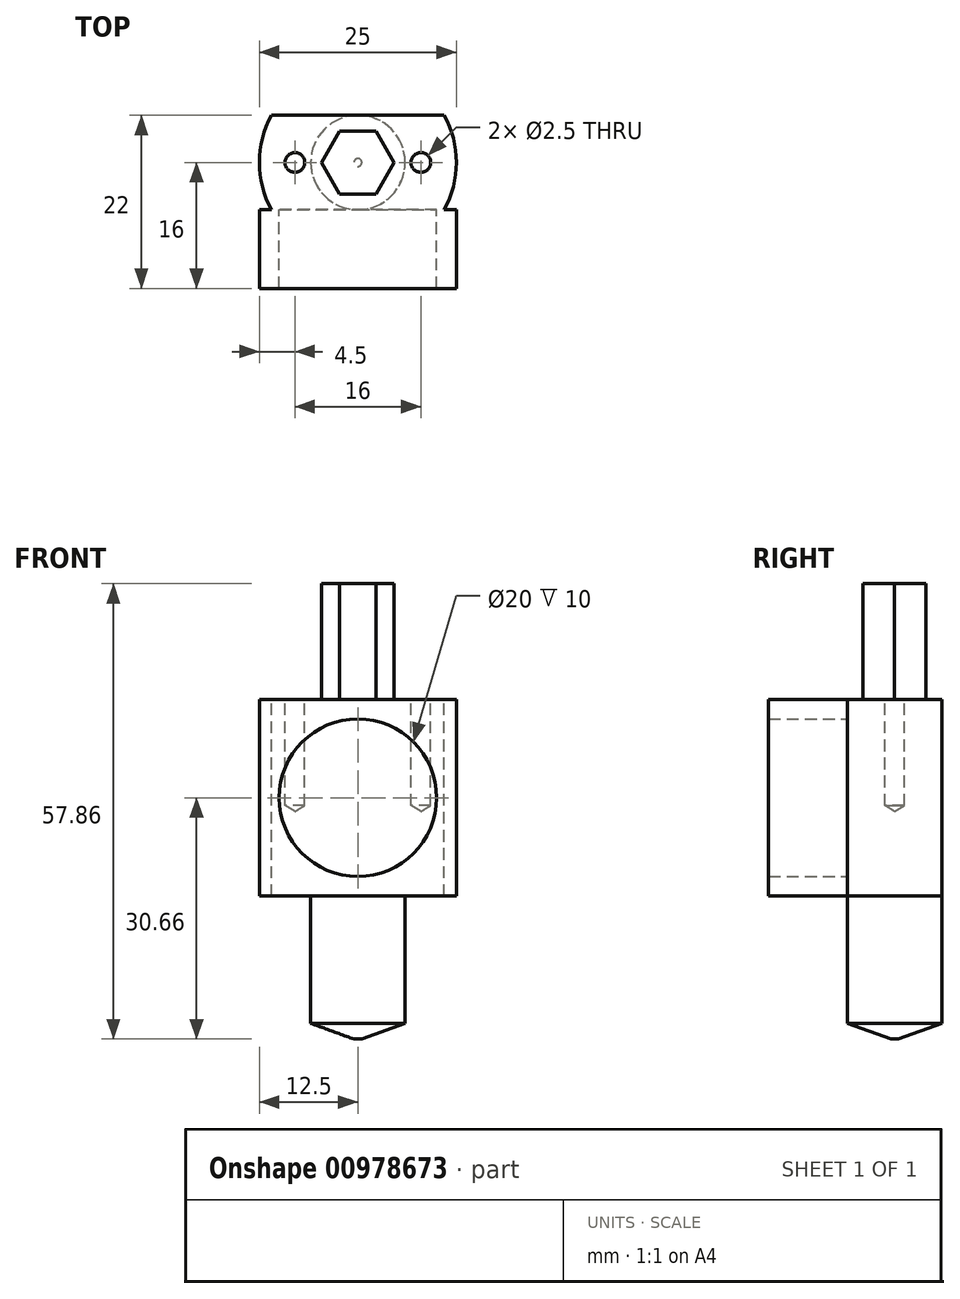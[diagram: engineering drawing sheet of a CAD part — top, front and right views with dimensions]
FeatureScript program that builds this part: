
annotation { "Feature Type Name" : "Feature", "Feature Type Description" : "" }
export const myFeature = defineFeature(function(context is Context, id is Id, definition is map)
    precondition{}
    {
        {
            var Q0;
            Q0=qCreatedBy(makeId("Top.planeOp"),FACE);
            var sketch = newSketch(context, id + "F0", { "sketchPlane" : qUnion([Q0])});
            skCircle(sketch, "E0", {"center": v(0, 0) * mm, "radius": 12.5 * mm});
            skLineSegment(sketch, "E1.bottom", {"start": v(-13, 6) * mm, "end": v(13, 6) * mm});
            skLineSegment(sketch, "E1.top", {"start": v(-13, -6) * mm, "end": v(13, -6) * mm});
            skLineSegment(sketch, "E1.left", {"start": v(-13, 6) * mm, "end": v(-13, -6) * mm});
            skLineSegment(sketch, "E1.right", {"start": v(13, 6) * mm, "end": v(13, -6) * mm});
            skPoint(sketch, "E2", {"position": v(0, 6) * mm});
            skPoint(sketch, "E3", {"position": v(-13, 0) * mm});
            skLineSegment(sketch, "E4", {"start": v(0, 6) * mm, "end": v(0, 0) * mm, "construction": true});
            skLineSegment(sketch, "E5", {"start": v(-13, 0) * mm, "end": v(0, 0) * mm, "construction": true});
            skSolve(sketch);
        }
        {
            var Q0;
            {var subQ0=sQuery(id+"F0.wireOp",EDGE,"E1.bottom");var subQ1=sQuery(id+"F0.wireOp",EDGE,"E0");var subQ2=makeQuery(id+"F0.imprint","INTERSECT",VERTEX,{"disambiguationData":[OD(0.0)],"derivedFrom":[subQ1,subQ0]});Q0=makeQuery(id+"F0.imprint","IMPRINT",FACE,{"disambiguationData":[TD([[makeQuery(id+"F0.imprint","IMPRINT",EDGE,{"disambiguationData":[TD([[subQ2,-1.0]])],"derivedFrom":subQ1}),1.0]])]});}
            extrude(context, id + "F1", {"entities" : qUnion([Q0]), "oppositeDirection" : true, "depth" : 25 * mm, "offsetDistance" : 25 * mm});
        }
        {
            var Q0;
            Q0=makeQuery(id+"F1.opExtrude","CAP_FACE",FACE,{"disambiguationData":[OSD([sQuery(id+"F0.wireOp",EDGE,"E0"),sQuery(id+"F0.wireOp",EDGE,"E1.bottom"),sQuery(id+"F0.wireOp",EDGE,"E1.top")])],"isStart":true});
            var sketch = newSketch(context, id + "F2", { "sketchPlane" : qUnion([Q0])});
            skLineSegment(sketch, "E6", {"start": v(-8, 0) * mm, "end": v(8, 0) * mm, "construction": true});
            skPoint(sketch, "E7", {"position": v(0, 0) * mm});
            skSolve(sketch);
        }
        {
            var Q0;
            Q0=sQuery(id+"F2.wireOp",VERTEX,"E6.start");
            var Q1;
            Q1=sQuery(id+"F2.wireOp",VERTEX,"E6.end");
            var Q2;
            Q2=makeQuery(id+"F1.opExtrude","SWEPT_BODY",BODY,{"disambiguationData":[OSD([sQuery(id+"F0.wireOp",EDGE,"E0"),sQuery(id+"F0.wireOp",EDGE,"E1.bottom"),sQuery(id+"F0.wireOp",EDGE,"E1.top")])]});
            hole(context, id + "F3", {"style" : HoleStyle.SIMPLE, "endStyle" : HoleEndStyle.BLIND, "standardTappedOrClearance" : lookupTablePath({ "standard" : "ISO", "engagement" : "75%", "pitch" : "0.5 mm", "size" : "M3", "type" : "Tapped" }), "standardBlindInLast" : lookupTablePath({ "standard" : "ISO", "fit" : "Normal", "engagement" : "75%", "pitch" : "0.5 mm", "size" : "M3", "type" : "Clearance & tapped" }), "holeDiameter" : 2.5 * mm, "majorDiameter" : 3 * mm, "showTappedDepth" : true, "holeDepth" : 13.5 * mm, "isTappedThrough" : true, "tappedDepth" : 12 * mm, "tapClearance" : 3, "startFromSketch" : true, "locations" : qUnion([Q0, Q1]), "scope" : qUnion([Q2])});
        }
        {
            var Q0;
            Q0=makeQuery(id+"F1.opExtrude","SWEPT_FACE",FACE,{"disambiguationData":[OSD([sQuery(id+"F0.wireOp",EDGE,"E1.top")])]});
            var sketch = newSketch(context, id + "F4", { "sketchPlane" : qUnion([Q0])});
            skLineSegment(sketch, "E8.bottom", {"start": v(-12.5, 0) * mm, "end": v(12.5, 0) * mm});
            skLineSegment(sketch, "E8.top", {"start": v(-12.5, -25) * mm, "end": v(12.5, -25) * mm});
            skLineSegment(sketch, "E8.left", {"start": v(-12.5, 0) * mm, "end": v(-12.5, -25) * mm});
            skLineSegment(sketch, "E8.right", {"start": v(12.5, 0) * mm, "end": v(12.5, -25) * mm});
            skPoint(sketch, "E9", {"position": v(0, 0) * mm});
            skPoint(sketch, "E10", {"position": v(-12.5, -12.5) * mm});
            skPoint(sketch, "E11", {"position": v(-10.97, -12.5) * mm});
            skLineSegment(sketch, "E12", {"start": v(-10.97, -12.5) * mm, "end": v(-12.5, -12.5) * mm, "construction": true});
            skCircle(sketch, "E13", {"center": v(0, -12.5) * mm, "radius": 10 * mm});
            skLineSegment(sketch, "E14", {"start": v(-10.97, -12.5) * mm, "end": v(0, -12.5) * mm, "construction": true});
            skSolve(sketch);
        }
        {
            var Q0;
            Q0=makeQuery(id+"F4.imprint","IMPRINT",FACE,{"disambiguationData":[TD([[makeQuery(id+"F4.imprint","IMPRINT",EDGE,{"derivedFrom":sQuery(id+"F4.wireOp",EDGE,"E13")}),-1.0]])]});
            var Q1;
            {var subQ4=sQuery(id+"F4.wireOp",EDGE,"E8.left");Q1=makeQuery(id+"F4.imprint","IMPRINT",FACE,{"disambiguationData":[TD([[makeQuery(id+"F4.imprint","IMPRINT",EDGE,{"derivedFrom":subQ4}),1.0]])]});}
            var Q2;
            {var subQ4=sQuery(id+"F4.wireOp",EDGE,"E8.right");Q2=makeQuery(id+"F4.imprint","IMPRINT",FACE,{"disambiguationData":[TD([[makeQuery(id+"F4.imprint","IMPRINT",EDGE,{"derivedFrom":subQ4}),-1.0]])]});}
            extrude(context, id + "F5", {"entities" : qUnion([Q0, Q1, Q2]), "operationType" : NewBodyOperationType.ADD, "depth" : 10 * mm, "offsetDistance" : 25 * mm});
        }
        {
            var Q0;
            Q0=makeQuery(id+"F5.boolean.opBoolean","MERGE",FACE,{"derivedFrom":[makeQuery(id+"F1.opExtrude","CAP_FACE",FACE,{"disambiguationData":[OSD([sQuery(id+"F0.wireOp",EDGE,"E0"),sQuery(id+"F0.wireOp",EDGE,"E1.bottom"),sQuery(id+"F0.wireOp",EDGE,"E1.top")])],"isStart":false}),makeQuery(id+"F5.opExtrude","SWEPT_FACE",FACE,{"disambiguationData":[OSD([sQuery(id+"F4.wireOp",EDGE,"E8.top")])]})]});
            var sketch = newSketch(context, id + "F6", { "sketchPlane" : qUnion([Q0])});
            skCircle(sketch, "E15", {"center": v(0, 0) * mm, "radius": 6 * mm});
            skSolve(sketch);
        }
        {
            var Q0;
            Q0=makeQuery(id+"F6.imprint","IMPRINT",FACE,{"disambiguationData":[TD([[makeQuery(id+"F6.imprint","IMPRINT",EDGE,{"derivedFrom":sQuery(id+"F6.wireOp",EDGE,"E15")}),1.0]])]});
            extrude(context, id + "F7", {"entities" : qUnion([Q0]), "operationType" : NewBodyOperationType.ADD, "depth" : (43.16 - 25) * mm, "offsetDistance" : 25 * mm});
        }
        {
            var Q0;
            Q0=makeQuery(id+"F7.opExtrude","CAP_EDGE",EDGE,{"disambiguationData":[OSD([sQuery(id+"F6.wireOp",EDGE,"E15")])],"isStart":false});
            chamfer(context, id + "F8", {"entities" : qUnion([Q0]), "chamferType" : ChamferType.TWO_OFFSETS, "width1" : 5.5 * mm, "oppositeDirection" : false, "width2" : 2 * mm, "tangentPropagation" : true});
        }
        {
            var Q0;
            Q0=makeQuery(id+"F5.boolean.opBoolean","MERGE",FACE,{"derivedFrom":[makeQuery(id+"F1.opExtrude","CAP_FACE",FACE,{"disambiguationData":[OSD([sQuery(id+"F0.wireOp",EDGE,"E0"),sQuery(id+"F0.wireOp",EDGE,"E1.bottom"),sQuery(id+"F0.wireOp",EDGE,"E1.top")])],"isStart":true}),makeQuery(id+"F5.opExtrude","SWEPT_FACE",FACE,{"disambiguationData":[OSD([sQuery(id+"F4.wireOp",EDGE,"E8.bottom")])]})]});
            var sketch = newSketch(context, id + "F9", { "sketchPlane" : qUnion([Q0])});
            skCircle(sketch, "E16.cCircle", {"center": v(0, 0) * mm, "radius": 4 * mm, "construction": true});
            skLineSegment(sketch, "E16.0", {"start": v(2.32, 4) * mm, "end": v(4.62, 0) * mm});
            skLineSegment(sketch, "E16.1", {"start": v(4.62, 0) * mm, "end": v(2.3, -4) * mm});
            skLineSegment(sketch, "E16.2", {"start": v(2.3, -4) * mm, "end": v(-2.32, -4) * mm});
            skLineSegment(sketch, "E16.3", {"start": v(-2.32, -4) * mm, "end": v(-4.62, 0) * mm});
            skLineSegment(sketch, "E16.4", {"start": v(-4.62, 0) * mm, "end": v(-2.3, 4) * mm});
            skLineSegment(sketch, "E16.5", {"start": v(-2.3, 4) * mm, "end": v(2.32, 4) * mm});
            skPoint(sketch, "E16.0.midPoint", {"position": v(3.47, 2) * mm});
            skSolve(sketch);
        }
        {
            var Q0;
            Q0=makeQuery(id+"F9.imprint","IMPRINT",FACE,{"disambiguationData":[TD([[makeQuery(id+"F9.imprint","IMPRINT",EDGE,{"derivedFrom":sQuery(id+"F9.wireOp",EDGE,"E16.0")}),-1.0]])]});
            extrude(context, id + "F10", {"entities" : qUnion([Q0]), "operationType" : NewBodyOperationType.ADD, "depth" : 14.7 * mm, "offsetDistance" : 25 * mm});
        }
    });
